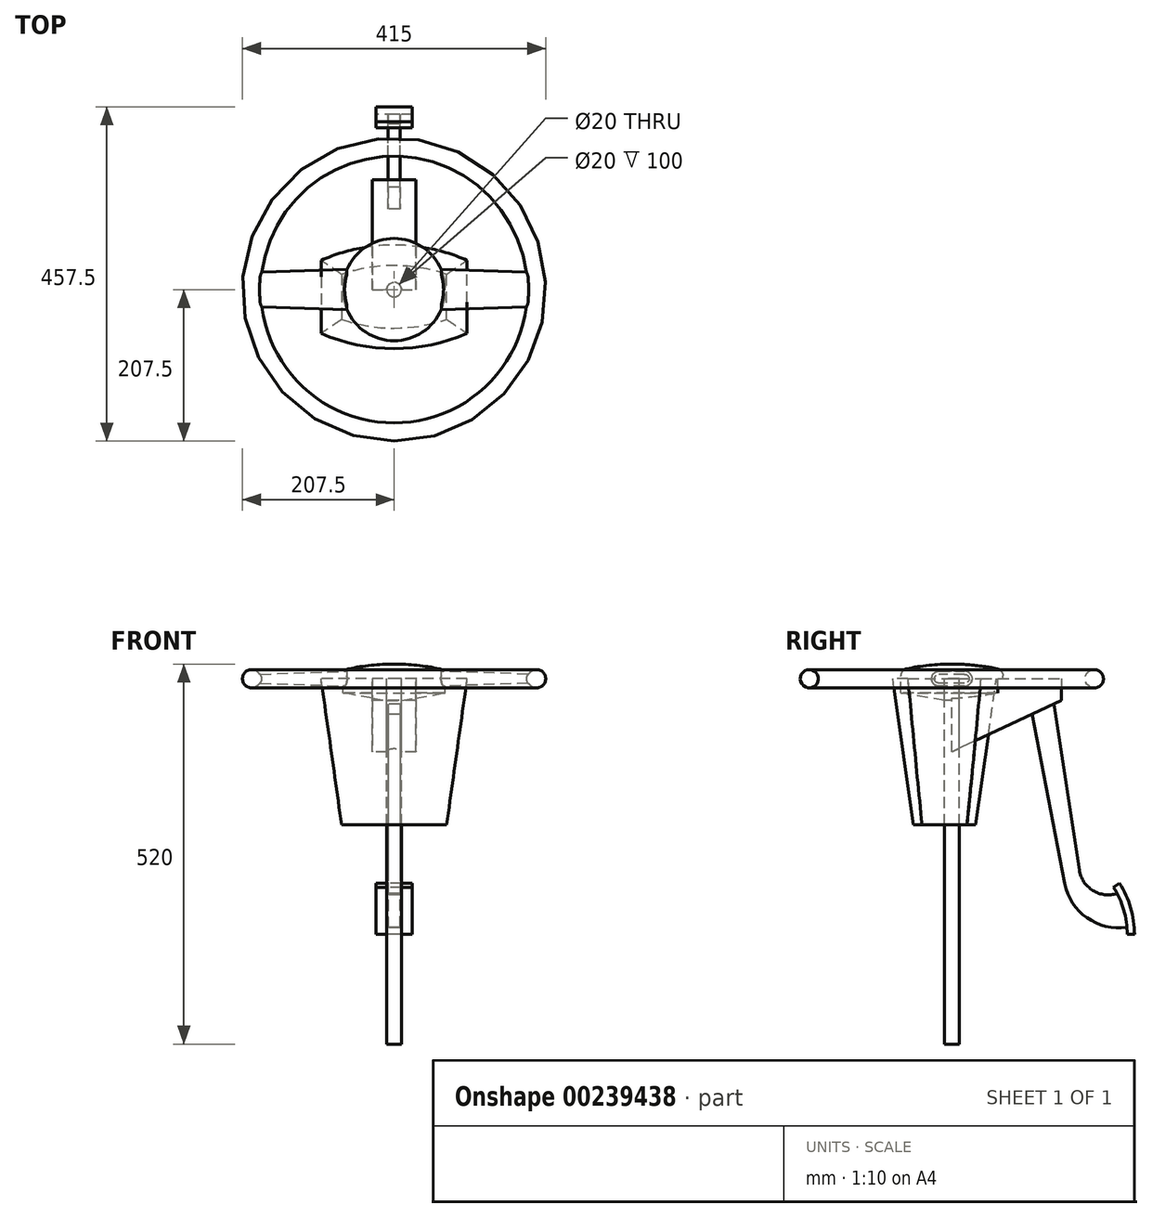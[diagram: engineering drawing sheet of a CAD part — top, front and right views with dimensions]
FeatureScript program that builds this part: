
annotation { "Feature Type Name" : "Feature", "Feature Type Description" : "" }
export const myFeature = defineFeature(function(context is Context, id is Id, definition is map)
    precondition{}
    {
        {
            var Q0;
            Q0=qCreatedBy(makeId("Right.planeOp"),FACE);
            var sketch = newSketch(context, id + "F0", { "sketchPlane" : qUnion([Q0])});
            skLineSegment(sketch, "E0", {"start": v(0, 0) * mm, "end": v(150, 0) * mm});
            skLineSegment(sketch, "E1", {"start": v(150, 0) * mm, "end": v(150, -30) * mm});
            skLineSegment(sketch, "E2", {"start": v(150, -30) * mm, "end": v(0, -100) * mm});
            skLineSegment(sketch, "E3", {"start": v(0, -100) * mm, "end": v(0, 0) * mm});
            skLineSegment(sketch, "E4", {"start": v(140, -34.67) * mm, "end": v(174.6, -261.9) * mm});
            skArc(sketch, "E5", {"start": v(174.6, -261.9) * mm, "mid": v(192.99, -289.81) * mm, "end": v(226.15, -294.03) * mm});
            skLineSegment(sketch, "E6", {"start": v(110, -48.67) * mm, "end": v(154.6, -280.07) * mm});
            skArc(sketch, "E7", {"start": v(154.6, -280.07) * mm, "mid": v(185.02, -327.16) * mm, "end": v(239.58, -340) * mm});
            skArc(sketch, "E8", {"start": v(240, -350) * mm, "mid": v(235.18, -316.34) * mm, "end": v(221.12, -285.38) * mm});
            skArc(sketch, "E9.0", {"start": v(250, -350) * mm, "mid": v(244.78, -313.54) * mm, "end": v(229.54, -280) * mm});
            skLineSegment(sketch, "E10", {"start": v(221.12, -285.38) * mm, "end": v(229.54, -280) * mm});
            skLineSegment(sketch, "E11", {"start": v(240, -350) * mm, "end": v(250, -350) * mm});
            skSolve(sketch);
        }
        {
            var Q0;
            Q0=makeQuery(id+"F0.imprint","IMPRINT",FACE,{"disambiguationData":[TD([[makeQuery(id+"F0.imprint","IMPRINT",EDGE,{"derivedFrom":sQuery(id+"F0.wireOp",EDGE,"E0")}),-1.0]])]});
            extrude(context, id + "F1", {"entities" : qUnion([Q0]), "endBound" : BoundingType.SYMMETRIC, "depth" : 60 * mm, "hasSecondDirection" : true, "secondDirectionOppositeDirection" : true, "secondDirectionDepth" : 25 * mm});
        }
        {
            var Q0;
            {var subQ1=sQuery(id+"F0.wireOp",EDGE,"E4");Q0=makeQuery(id+"F0.imprint","IMPRINT",FACE,{"disambiguationData":[TD([[makeQuery(id+"F0.imprint","IMPRINT",EDGE,{"derivedFrom":subQ1}),-1.0]])]});}
            extrude(context, id + "F2", {"entities" : qUnion([Q0]), "operationType" : NewBodyOperationType.ADD, "endBound" : BoundingType.SYMMETRIC, "depth" : 16 * mm});
        }
        {
            var Q0;
            Q0=makeQuery(id+"F0.imprint","IMPRINT",FACE,{"disambiguationData":[TD([[makeQuery(id+"F0.imprint","IMPRINT",EDGE,{"derivedFrom":sQuery(id+"F0.wireOp",EDGE,"E9.0")}),1.0]])]});
            extrude(context, id + "F3", {"entities" : qUnion([Q0]), "operationType" : NewBodyOperationType.ADD, "endBound" : BoundingType.SYMMETRIC, "depth" : 50 * mm});
        }
        {
            var Q0;
            Q0=qCreatedBy(makeId("Right.planeOp"),FACE);
            var sketch = newSketch(context, id + "F4", { "sketchPlane" : qUnion([Q0])});
            skCircle(sketch, "E12", {"center": v(-195, 0) * mm, "radius": 12.5 * mm});
            skLineSegment(sketch, "E13", {"start": v(0, 20) * mm, "end": v(0, -500) * mm});
            skLineSegment(sketch, "E14", {"start": v(0, -500) * mm, "end": v(-10, -500) * mm});
            skLineSegment(sketch, "E15", {"start": v(-70, -19.42) * mm, "end": v(-70, 3.73) * mm});
            skLineSegment(sketch, "E16", {"start": v(0, 12.5) * mm, "end": v(-17.5, 12.5) * mm});
            skLineSegment(sketch, "E17", {"start": v(-17.5, -12.5) * mm, "end": v(0, -12.5) * mm});
            skArc(sketch, "E18", {"start": v(-17.5, 12.5) * mm, "mid": v(-30, 0) * mm, "end": v(-17.5, -12.5) * mm});
            skArc(sketch, "E19", {"start": v(0, 20) * mm, "mid": v(-31.2, 18.37) * mm, "end": v(-62.07, 13.5) * mm});
            skLineSegment(sketch, "E20", {"start": v(-70, -19.42) * mm, "end": v(-10, -30) * mm});
            skLineSegment(sketch, "E21", {"start": v(-10, -30) * mm, "end": v(-10, -500) * mm});
            skLineSegment(sketch, "E22.MirrorCS", {"start": v(0, 12.5) * mm, "end": v(17.5, 12.5) * mm});
            skLineSegment(sketch, "E23.MirrorCS", {"start": v(17.5, -12.5) * mm, "end": v(0, -12.5) * mm});
            skArc(sketch, "E24.MirrorCS", {"start": v(17.5, 12.5) * mm, "mid": v(30, 0) * mm, "end": v(17.5, -12.5) * mm});
            skPoint(sketch, "E25.visualSharp", {"position": v(-70, 11.72) * mm});
            skArc(sketch, "E25.filletArc", {"start": v(-62.07, 13.5) * mm, "mid": v(-67.77, 10.02) * mm, "end": v(-70, 3.73) * mm});
            skSolve(sketch);
        }
        {
            var Q0;
            Q0=makeQuery(id+"F4.imprint","IMPRINT",FACE,{"disambiguationData":[TD([[makeQuery(id+"F4.imprint","IMPRINT",EDGE,{"derivedFrom":sQuery(id+"F4.wireOp",EDGE,"E12")}),1.0]])]});
            var Q1;
            Q1=sQuery(id+"F4.wireOp",EDGE,"E13");
            revolve(context, id + "F5", {"entities" : qUnion([Q0]), "axis" : qUnion([Q1]), "revolveType" : RevolveType.FULL});
        }
        {
            var Q0;
            {var subQ0=sQuery(id+"F4.wireOp",EDGE,"E16");Q0=makeQuery(id+"F4.imprint","IMPRINT",FACE,{"disambiguationData":[TD([[makeQuery(id+"F4.imprint","IMPRINT",EDGE,{"derivedFrom":subQ0}),1.0]])]});}
            var Q1;
            {var subQ0=sQuery(id+"F4.wireOp",EDGE,"E22.MirrorCS");Q1=makeQuery(id+"F4.imprint","IMPRINT",FACE,{"disambiguationData":[TD([[makeQuery(id+"F4.imprint","IMPRINT",EDGE,{"derivedFrom":subQ0}),-1.0]])]});}
            var Q2;
            Q2=makeQuery(id+"F5.opRevolve","SWEPT_FACE",FACE,{"disambiguationData":[OSD([sQuery(id+"F4.wireOp",EDGE,"E12")])]});
            var Q3;
            Q3=makeQuery(id+"F5.opRevolve","SWEPT_FACE",FACE,{"disambiguationData":[OSD([sQuery(id+"F4.wireOp",EDGE,"E12")])]});
            extrude(context, id + "F6", {"entities" : qUnion([Q0, Q1]), "operationType" : NewBodyOperationType.ADD, "endBound" : BoundingType.UP_TO_SURFACE, "endBoundEntityFace" : qUnion([Q2]), "depth" : 25 * mm, "hasDraft" : true, "draftAngle" : 2 * degree, "draftPullDirection" : true, "hasSecondDirection" : true, "secondDirectionBound" : SecondDirectionBoundingType.UP_TO_SURFACE, "secondDirectionOppositeDirection" : true, "secondDirectionBoundEntityFace" : qUnion([Q3]), "secondDirectionDepth" : 25 * mm, "hasSecondDirectionDraft" : true, "secondDirectionDraftAngle" : 2 * degree, "secondDirectionDraftPullDirection" : true});
        }
        {
            var Q0;
            {var subQ0=sQuery(id+"F4.wireOp",EDGE,"E14");Q0=makeQuery(id+"F4.imprint","IMPRINT",FACE,{"disambiguationData":[TD([[makeQuery(id+"F4.imprint","IMPRINT",EDGE,{"derivedFrom":subQ0}),-1.0]])]});}
            var Q1;
            {var subQ0=sQuery(id+"F4.wireOp",EDGE,"E16");Q1=makeQuery(id+"F4.imprint","IMPRINT",FACE,{"disambiguationData":[TD([[makeQuery(id+"F4.imprint","IMPRINT",EDGE,{"derivedFrom":subQ0}),1.0]])]});}
            var Q2;
            Q2=sQuery(id+"F4.wireOp",EDGE,"E13");
            revolve(context, id + "F7", {"operationType" : NewBodyOperationType.ADD, "entities" : qUnion([Q0, Q1]), "axis" : qUnion([Q2]), "revolveType" : RevolveType.FULL});
        }
        {
            var Q0;
            Q0=qCreatedBy(makeId("Top.planeOp"),FACE);
            var sketch = newSketch(context, id + "F8", { "sketchPlane" : qUnion([Q0])});
            skLineSegment(sketch, "E26", {"start": v(-100, 40) * mm, "end": v(-100, -60) * mm});
            skLineSegment(sketch, "E27", {"start": v(100, -60) * mm, "end": v(100, 40) * mm});
            skArc(sketch, "E28", {"start": v(100, 40) * mm, "mid": v(0, 60.87) * mm, "end": v(-100, 40) * mm});
            skArc(sketch, "E29", {"start": v(-100, -60) * mm, "mid": v(0, -80.87) * mm, "end": v(100, -60) * mm});
            skLineSegment(sketch, "E30", {"start": v(0, 0) * mm, "end": v(0, -49.82) * mm, "construction": true});
            skCircle(sketch, "E31", {"center": v(0, 0) * mm, "radius": 10 * mm});
            skLineSegment(sketch, "E32", {"start": v(0, 0) * mm, "end": v(-58.76, 0) * mm, "construction": true});
            skSolve(sketch);
        }
        {
            var Q0;
            Q0=makeQuery(id+"F8.imprint","IMPRINT",FACE,{"disambiguationData":[TD([[makeQuery(id+"F8.imprint","IMPRINT",EDGE,{"derivedFrom":sQuery(id+"F8.wireOp",EDGE,"E26")}),1.0]])]});
            var Q1;
            Q1=makeQuery(id+"F8.imprint","IMPRINT",FACE,{"disambiguationData":[TD([[makeQuery(id+"F8.imprint","IMPRINT",EDGE,{"derivedFrom":sQuery(id+"F8.wireOp",EDGE,"E31")}),1.0]])]});
            extrude(context, id + "F9", {"entities" : qUnion([Q0, Q1]), "oppositeDirection" : true, "depth" : 200 * mm, "hasDraft" : true, "draftAngle" : 8 * degree, "draftPullDirection" : true});
        }
        {
            var Q0;
            Q0=makeQuery(id+"F8.imprint","IMPRINT",FACE,{"disambiguationData":[TD([[makeQuery(id+"F8.imprint","IMPRINT",EDGE,{"derivedFrom":sQuery(id+"F8.wireOp",EDGE,"E31")}),1.0]])]});
            var Q1;
            Q1=makeQuery(id+"F9.opExtrude","CAP_FACE",FACE,{"disambiguationData":[OSD([sQuery(id+"F8.wireOp",EDGE,"E26"),sQuery(id+"F8.wireOp",EDGE,"E27"),sQuery(id+"F8.wireOp",EDGE,"E28"),sQuery(id+"F8.wireOp",EDGE,"E29")])],"isStart":false});
            extrude(context, id + "F10", {"entities" : qUnion([Q0]), "operationType" : NewBodyOperationType.REMOVE, "endBound" : BoundingType.UP_TO_SURFACE, "oppositeDirection" : true, "endBoundEntityFace" : qUnion([Q1]), "depth" : 25 * mm});
        }
    });
